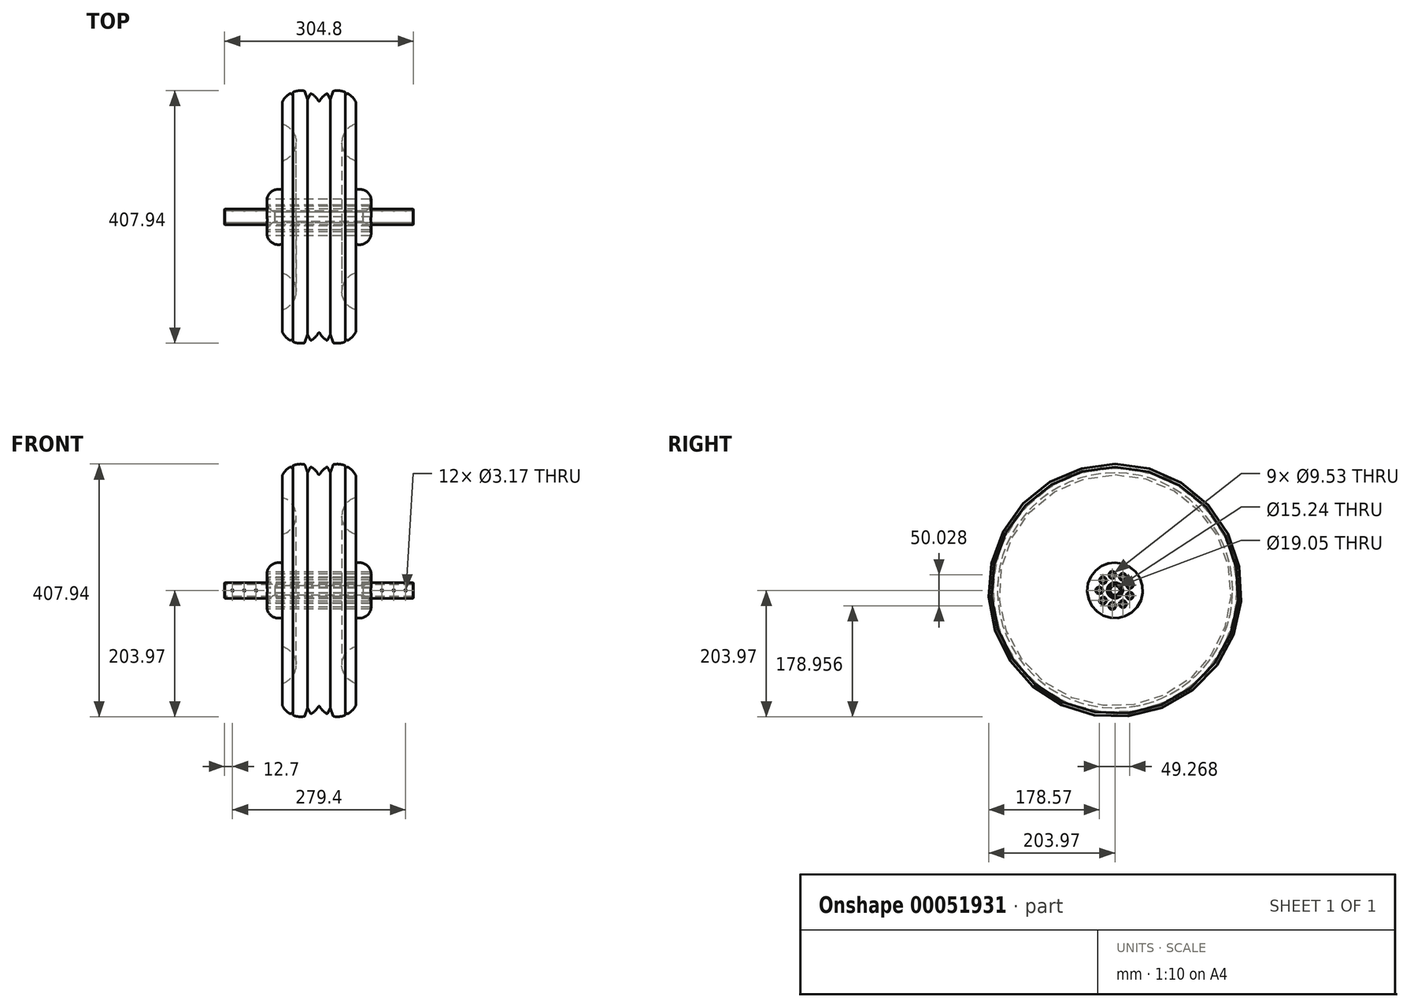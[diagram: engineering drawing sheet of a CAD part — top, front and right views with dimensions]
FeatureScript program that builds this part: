
annotation { "Feature Type Name" : "Feature", "Feature Type Description" : "" }
export const myFeature = defineFeature(function(context is Context, id is Id, definition is map)
    precondition{}
    {
        {
            var Q0;
            Q0=qCreatedBy(makeId("Right.planeOp"),FACE);
            var sketch = newSketch(context, id + "F0", { "sketchPlane" : qUnion([Q0])});
            skCircle(sketch, "E0", {"center": v(0, 0) * mm, "radius": 12.7 * mm});
            skCircle(sketch, "E1", {"center": v(0, 0) * mm, "radius": 9.53 * mm});
            skSolve(sketch);
        }
        {
            var Q0;
            Q0=makeQuery(id+"F0.imprint","IMPRINT",FACE,{"disambiguationData":[TD([[makeQuery(id+"F0.imprint","IMPRINT",EDGE,{"derivedFrom":sQuery(id+"F0.wireOp",EDGE,"E0")}),1.0]])]});
            extrude(context, id + "F1", {"entities" : qUnion([Q0]), "endBound" : BoundingType.SYMMETRIC, "depth" : 304.8 * mm});
        }
        {
            var Q0;
            Q0=qCreatedBy(makeId("Front.planeOp"),FACE);
            var sketch = newSketch(context, id + "F2", { "sketchPlane" : qUnion([Q0])});
            skArc(sketch, "E2", {"start": v(-59.42, 43.9) * mm, "mid": v(-83.37, 31.57) * mm, "end": v(-71.03, 7.62) * mm});
            skArc(sketch, "E3", {"start": v(0, 185.42) * mm, "mid": v(-5.59, 193.52) * mm, "end": v(-13.3, 199.62) * mm});
            skLineSegment(sketch, "E4", {"start": v(-71.03, 7.62) * mm, "end": v(0, 7.62) * mm});
            skLineSegment(sketch, "E5", {"start": v(0, 7.62) * mm, "end": v(0, -76.85) * mm, "construction": true});
            skArc(sketch, "E6.MirrorCS", {"start": v(0, 185.42) * mm, "mid": v(5.59, 193.52) * mm, "end": v(13.3, 199.62) * mm});
            skArc(sketch, "E7.MirrorCS", {"start": v(59.42, 43.9) * mm, "mid": v(83.37, 31.57) * mm, "end": v(71.03, 7.62) * mm});
            skLineSegment(sketch, "E8.MirrorCS", {"start": v(71.03, 7.62) * mm, "end": v(0, 7.62) * mm});
            skLineSegment(sketch, "E9", {"start": v(-111.33, 0) * mm, "end": v(105.13, 0) * mm, "construction": true});
            skLineSegment(sketch, "E10", {"start": v(-46.26, 199.53) * mm, "end": v(-42.37, 196.5) * mm});
            skLineSegment(sketch, "E11", {"start": v(-42.37, 196.5) * mm, "end": v(-42.37, 201.45) * mm});
            skArc(sketch, "E12.trimOffspring", {"start": v(-46.26, 199.53) * mm, "mid": v(-53.9, 193.46) * mm, "end": v(-59.42, 185.42) * mm});
            skLineSegment(sketch, "E13", {"start": v(-23, 203.29) * mm, "end": v(-18.35, 189.78) * mm});
            skLineSegment(sketch, "E14", {"start": v(-18.35, 189.78) * mm, "end": v(-13.3, 199.62) * mm});
            skArc(sketch, "E15.trimOffspring", {"start": v(-23, 203.29) * mm, "mid": v(-32.82, 203.83) * mm, "end": v(-42.37, 201.45) * mm});
            skArc(sketch, "E16.MirrorCS", {"start": v(46.26, 199.53) * mm, "mid": v(53.9, 193.46) * mm, "end": v(59.42, 185.42) * mm});
            skLineSegment(sketch, "E17.MirrorCS", {"start": v(46.26, 199.53) * mm, "end": v(42.37, 196.5) * mm});
            skLineSegment(sketch, "E18.MirrorCS", {"start": v(42.37, 196.5) * mm, "end": v(42.37, 201.45) * mm});
            skLineSegment(sketch, "E19.MirrorCS", {"start": v(23, 203.29) * mm, "end": v(18.35, 189.78) * mm});
            skLineSegment(sketch, "E20.MirrorCS", {"start": v(18.35, 189.78) * mm, "end": v(13.3, 199.62) * mm});
            skArc(sketch, "E21.trimOffspring", {"start": v(23, 203.29) * mm, "mid": v(32.82, 203.83) * mm, "end": v(42.37, 201.45) * mm});
            skLineSegment(sketch, "E22", {"start": v(-59.42, 43.9) * mm, "end": v(-59.42, 90.42) * mm});
            skLineSegment(sketch, "E23", {"start": v(59.42, 185.42) * mm, "end": v(59.42, 150.1) * mm});
            skArc(sketch, "E24", {"start": v(-59.42, 90.42) * mm, "mid": v(-36.85, 120.26) * mm, "end": v(-59.42, 150.1) * mm});
            skLineSegment(sketch, "E25.trimOffspring", {"start": v(-59.42, 150.1) * mm, "end": v(-59.42, 185.42) * mm});
            skPoint(sketch, "E26.orphan", {"position": v(0, 77.88) * mm});
            skArc(sketch, "E27.MirrorCS", {"start": v(59.42, 90.42) * mm, "mid": v(36.85, 120.26) * mm, "end": v(59.42, 150.1) * mm});
            skLineSegment(sketch, "E28.trimOffspring", {"start": v(59.42, 90.42) * mm, "end": v(59.42, 43.9) * mm});
            skSolve(sketch);
        }
        {
            var Q0;
            Q0=makeQuery(id+"F2.imprint","IMPRINT",FACE,{"disambiguationData":[TD([[makeQuery(id+"F2.imprint","IMPRINT",EDGE,{"derivedFrom":sQuery(id+"F2.wireOp",EDGE,"E2")}),1.0]])]});
            var Q1;
            Q1=sQuery(id+"F2.wireOp",EDGE,"E9");
            revolve(context, id + "F3", {"entities" : qUnion([Q0]), "axis" : qUnion([Q1]), "revolveType" : RevolveType.FULL});
        }
        {
            var Q0;
            Q0=qCreatedBy(makeId("Right.planeOp"),FACE);
            var sketch = newSketch(context, id + "F4", { "sketchPlane" : qUnion([Q0])});
            skCircle(sketch, "E29", {"center": v(-25.4, 0) * mm, "radius": 4.76 * mm});
            skCircle(sketch, "E30.1.0", {"center": v(-19.46, -16.33) * mm, "radius": 4.76 * mm});
            skCircle(sketch, "E30.2.0", {"center": v(-4.41, -25.01) * mm, "radius": 4.76 * mm});
            skCircle(sketch, "E30.3.0", {"center": v(12.7, -22) * mm, "radius": 4.76 * mm});
            skCircle(sketch, "E30.4.0", {"center": v(23.87, -8.69) * mm, "radius": 4.76 * mm});
            skCircle(sketch, "E30.5.0", {"center": v(23.87, 8.69) * mm, "radius": 4.76 * mm});
            skCircle(sketch, "E30.6.0", {"center": v(12.7, 22) * mm, "radius": 4.76 * mm});
            skCircle(sketch, "E30.7.0", {"center": v(-4.41, 25.01) * mm, "radius": 4.76 * mm});
            skCircle(sketch, "E30.8.0", {"center": v(-19.46, 16.33) * mm, "radius": 4.76 * mm});
            skPoint(sketch, "E30.center", {"position": v(0, 0) * mm});
            skSolve(sketch);
        }
        {
            var Q0;
            Q0 = qSketchRegion(id + "F4", true);
            extrude(context, id + "F5", {"entities" : qUnion([Q0]), "operationType" : NewBodyOperationType.REMOVE, "endBound" : BoundingType.THROUGH_ALL, "depth" : 25.4 * mm, "hasSecondDirection" : true, "secondDirectionBound" : SecondDirectionBoundingType.THROUGH_ALL, "secondDirectionOppositeDirection" : true, "secondDirectionDepth" : 25.4 * mm});
        }
        {
            var Q0;
            Q0=makeQuery(id+"F1.opExtrude","CAP_EDGE",EDGE,{"disambiguationData":[OSD([sQuery(id+"F0.wireOp",EDGE,"E1")])],"isStart":false});
            var Q1;
            Q1=makeQuery(id+"F1.opExtrude","CAP_EDGE",EDGE,{"disambiguationData":[OSD([sQuery(id+"F0.wireOp",EDGE,"E0")])],"isStart":false});
            var Q2;
            Q2=makeQuery(id+"F1.opExtrude","CAP_EDGE",EDGE,{"disambiguationData":[OSD([sQuery(id+"F0.wireOp",EDGE,"E0")])],"isStart":true});
            var Q3;
            Q3=makeQuery(id+"F1.opExtrude","CAP_EDGE",EDGE,{"disambiguationData":[OSD([sQuery(id+"F0.wireOp",EDGE,"E1")])],"isStart":true});
            chamfer(context, id + "F6", {"entities" : qUnion([Q0, Q1, Q2, Q3]), "width" : 0.76 * mm, "tangentPropagation" : true});
        }
        {
            var Q0;
            Q0=makeQuery(id+"F5.boolean.opBoolean","INTERSECT",EDGE,{"derivedFrom":[makeQuery(id+"F3.opRevolve","SWEPT_FACE",FACE,{"disambiguationData":[OSD([sQuery(id+"F2.wireOp",EDGE,"E7.MirrorCS")])]}),makeQuery(id+"F5.opExtrude","SWEPT_FACE",FACE,{"disambiguationData":[OSD([sQuery(id+"F4.wireOp",EDGE,"E30.5.0")])]})]});
            var Q1;
            Q1=makeQuery(id+"F5.boolean.opBoolean","INTERSECT",EDGE,{"derivedFrom":[makeQuery(id+"F3.opRevolve","SWEPT_FACE",FACE,{"disambiguationData":[OSD([sQuery(id+"F2.wireOp",EDGE,"E7.MirrorCS")])]}),makeQuery(id+"F5.opExtrude","SWEPT_FACE",FACE,{"disambiguationData":[OSD([sQuery(id+"F4.wireOp",EDGE,"E30.4.0")])]})]});
            var Q2;
            Q2=makeQuery(id+"F5.boolean.opBoolean","INTERSECT",EDGE,{"derivedFrom":[makeQuery(id+"F3.opRevolve","SWEPT_FACE",FACE,{"disambiguationData":[OSD([sQuery(id+"F2.wireOp",EDGE,"E7.MirrorCS")])]}),makeQuery(id+"F5.opExtrude","SWEPT_FACE",FACE,{"disambiguationData":[OSD([sQuery(id+"F4.wireOp",EDGE,"E30.6.0")])]})]});
            var Q3;
            Q3=makeQuery(id+"F5.boolean.opBoolean","INTERSECT",EDGE,{"derivedFrom":[makeQuery(id+"F3.opRevolve","SWEPT_FACE",FACE,{"disambiguationData":[OSD([sQuery(id+"F2.wireOp",EDGE,"E7.MirrorCS")])]}),makeQuery(id+"F5.opExtrude","SWEPT_FACE",FACE,{"disambiguationData":[OSD([sQuery(id+"F4.wireOp",EDGE,"E30.7.0")])]})]});
            var Q4;
            Q4=makeQuery(id+"F5.boolean.opBoolean","INTERSECT",EDGE,{"derivedFrom":[makeQuery(id+"F3.opRevolve","SWEPT_FACE",FACE,{"disambiguationData":[OSD([sQuery(id+"F2.wireOp",EDGE,"E7.MirrorCS")])]}),makeQuery(id+"F5.opExtrude","SWEPT_FACE",FACE,{"disambiguationData":[OSD([sQuery(id+"F4.wireOp",EDGE,"E30.8.0")])]})]});
            var Q5;
            Q5=makeQuery(id+"F5.boolean.opBoolean","INTERSECT",EDGE,{"derivedFrom":[makeQuery(id+"F3.opRevolve","SWEPT_FACE",FACE,{"disambiguationData":[OSD([sQuery(id+"F2.wireOp",EDGE,"E7.MirrorCS")])]}),makeQuery(id+"F5.opExtrude","SWEPT_FACE",FACE,{"disambiguationData":[OSD([sQuery(id+"F4.wireOp",EDGE,"E29")])]})]});
            var Q6;
            Q6=makeQuery(id+"F5.boolean.opBoolean","INTERSECT",EDGE,{"derivedFrom":[makeQuery(id+"F3.opRevolve","SWEPT_FACE",FACE,{"disambiguationData":[OSD([sQuery(id+"F2.wireOp",EDGE,"E7.MirrorCS")])]}),makeQuery(id+"F5.opExtrude","SWEPT_FACE",FACE,{"disambiguationData":[OSD([sQuery(id+"F4.wireOp",EDGE,"E30.1.0")])]})]});
            var Q7;
            Q7=makeQuery(id+"F5.boolean.opBoolean","INTERSECT",EDGE,{"derivedFrom":[makeQuery(id+"F3.opRevolve","SWEPT_FACE",FACE,{"disambiguationData":[OSD([sQuery(id+"F2.wireOp",EDGE,"E7.MirrorCS")])]}),makeQuery(id+"F5.opExtrude","SWEPT_FACE",FACE,{"disambiguationData":[OSD([sQuery(id+"F4.wireOp",EDGE,"E30.2.0")])]})]});
            var Q8;
            Q8=makeQuery(id+"F5.boolean.opBoolean","INTERSECT",EDGE,{"derivedFrom":[makeQuery(id+"F3.opRevolve","SWEPT_FACE",FACE,{"disambiguationData":[OSD([sQuery(id+"F2.wireOp",EDGE,"E7.MirrorCS")])]}),makeQuery(id+"F5.opExtrude","SWEPT_FACE",FACE,{"disambiguationData":[OSD([sQuery(id+"F4.wireOp",EDGE,"E30.3.0")])]})]});
            var Q9;
            Q9=makeQuery(id+"F5.boolean.opBoolean","INTERSECT",EDGE,{"derivedFrom":[makeQuery(id+"F3.opRevolve","SWEPT_FACE",FACE,{"disambiguationData":[OSD([sQuery(id+"F2.wireOp",EDGE,"E2")])]}),makeQuery(id+"F5.opExtrude","SWEPT_FACE",FACE,{"disambiguationData":[OSD([sQuery(id+"F4.wireOp",EDGE,"E30.4.0")])]})]});
            var Q10;
            Q10=makeQuery(id+"F5.boolean.opBoolean","INTERSECT",EDGE,{"derivedFrom":[makeQuery(id+"F3.opRevolve","SWEPT_FACE",FACE,{"disambiguationData":[OSD([sQuery(id+"F2.wireOp",EDGE,"E2")])]}),makeQuery(id+"F5.opExtrude","SWEPT_FACE",FACE,{"disambiguationData":[OSD([sQuery(id+"F4.wireOp",EDGE,"E30.5.0")])]})]});
            var Q11;
            Q11=makeQuery(id+"F5.boolean.opBoolean","INTERSECT",EDGE,{"derivedFrom":[makeQuery(id+"F3.opRevolve","SWEPT_FACE",FACE,{"disambiguationData":[OSD([sQuery(id+"F2.wireOp",EDGE,"E2")])]}),makeQuery(id+"F5.opExtrude","SWEPT_FACE",FACE,{"disambiguationData":[OSD([sQuery(id+"F4.wireOp",EDGE,"E30.6.0")])]})]});
            var Q12;
            Q12=makeQuery(id+"F5.boolean.opBoolean","INTERSECT",EDGE,{"derivedFrom":[makeQuery(id+"F3.opRevolve","SWEPT_FACE",FACE,{"disambiguationData":[OSD([sQuery(id+"F2.wireOp",EDGE,"E2")])]}),makeQuery(id+"F5.opExtrude","SWEPT_FACE",FACE,{"disambiguationData":[OSD([sQuery(id+"F4.wireOp",EDGE,"E30.7.0")])]})]});
            var Q13;
            Q13=makeQuery(id+"F5.boolean.opBoolean","INTERSECT",EDGE,{"derivedFrom":[makeQuery(id+"F3.opRevolve","SWEPT_FACE",FACE,{"disambiguationData":[OSD([sQuery(id+"F2.wireOp",EDGE,"E2")])]}),makeQuery(id+"F5.opExtrude","SWEPT_FACE",FACE,{"disambiguationData":[OSD([sQuery(id+"F4.wireOp",EDGE,"E30.8.0")])]})]});
            var Q14;
            Q14=makeQuery(id+"F5.boolean.opBoolean","INTERSECT",EDGE,{"derivedFrom":[makeQuery(id+"F3.opRevolve","SWEPT_FACE",FACE,{"disambiguationData":[OSD([sQuery(id+"F2.wireOp",EDGE,"E2")])]}),makeQuery(id+"F5.opExtrude","SWEPT_FACE",FACE,{"disambiguationData":[OSD([sQuery(id+"F4.wireOp",EDGE,"E29")])]})]});
            var Q15;
            Q15=makeQuery(id+"F5.boolean.opBoolean","INTERSECT",EDGE,{"derivedFrom":[makeQuery(id+"F3.opRevolve","SWEPT_FACE",FACE,{"disambiguationData":[OSD([sQuery(id+"F2.wireOp",EDGE,"E2")])]}),makeQuery(id+"F5.opExtrude","SWEPT_FACE",FACE,{"disambiguationData":[OSD([sQuery(id+"F4.wireOp",EDGE,"E30.1.0")])]})]});
            var Q16;
            Q16=makeQuery(id+"F5.boolean.opBoolean","INTERSECT",EDGE,{"derivedFrom":[makeQuery(id+"F3.opRevolve","SWEPT_FACE",FACE,{"disambiguationData":[OSD([sQuery(id+"F2.wireOp",EDGE,"E2")])]}),makeQuery(id+"F5.opExtrude","SWEPT_FACE",FACE,{"disambiguationData":[OSD([sQuery(id+"F4.wireOp",EDGE,"E30.2.0")])]})]});
            var Q17;
            Q17=makeQuery(id+"F5.boolean.opBoolean","INTERSECT",EDGE,{"derivedFrom":[makeQuery(id+"F3.opRevolve","SWEPT_FACE",FACE,{"disambiguationData":[OSD([sQuery(id+"F2.wireOp",EDGE,"E2")])]}),makeQuery(id+"F5.opExtrude","SWEPT_FACE",FACE,{"disambiguationData":[OSD([sQuery(id+"F4.wireOp",EDGE,"E30.3.0")])]})]});
            fillet(context, id + "F7", {"entities" : qUnion([Q0, Q1, Q2, Q3, Q4, Q5, Q6, Q7, Q8, Q9, Q10, Q11, Q12, Q13, Q14, Q15, Q16, Q17]), "radius" : 0.76 * mm, "tangentPropagation" : true, "allowEdgeOverflow" : false});
        }
        {
            var Q0;
            Q0=makeQuery(id+"F3.opRevolve","SWEPT_EDGE",EDGE,{"disambiguationData":[OSD([sQuery(id+"F2.wireOp",EDGE,"E12.trimOffspring"),sQuery(id+"F2.wireOp",EDGE,"E25.trimOffspring")])]});
            var Q1;
            Q1=makeQuery(id+"F3.opRevolve","SWEPT_EDGE",EDGE,{"disambiguationData":[OSD([sQuery(id+"F2.wireOp",EDGE,"E24"),sQuery(id+"F2.wireOp",EDGE,"E25.trimOffspring")])]});
            var Q2;
            Q2=makeQuery(id+"F3.opRevolve","SWEPT_EDGE",EDGE,{"disambiguationData":[OSD([sQuery(id+"F2.wireOp",EDGE,"E22"),sQuery(id+"F2.wireOp",EDGE,"E24")])]});
            var Q3;
            Q3=makeQuery(id+"F3.opRevolve","SWEPT_EDGE",EDGE,{"disambiguationData":[OSD([sQuery(id+"F2.wireOp",EDGE,"E2"),sQuery(id+"F2.wireOp",EDGE,"E22")])]});
            var Q4;
            Q4=makeQuery(id+"F3.opRevolve","SWEPT_EDGE",EDGE,{"disambiguationData":[OSD([sQuery(id+"F2.wireOp",EDGE,"E10"),sQuery(id+"F2.wireOp",EDGE,"E12.trimOffspring")])]});
            var Q5;
            Q5=makeQuery(id+"F3.opRevolve","SWEPT_EDGE",EDGE,{"disambiguationData":[OSD([sQuery(id+"F2.wireOp",EDGE,"E11"),sQuery(id+"F2.wireOp",EDGE,"E15.trimOffspring")])]});
            var Q6;
            Q6=makeQuery(id+"F3.opRevolve","SWEPT_EDGE",EDGE,{"disambiguationData":[OSD([sQuery(id+"F2.wireOp",EDGE,"E13"),sQuery(id+"F2.wireOp",EDGE,"E15.trimOffspring")])]});
            var Q7;
            Q7=makeQuery(id+"F3.opRevolve","SWEPT_EDGE",EDGE,{"disambiguationData":[OSD([sQuery(id+"F2.wireOp",EDGE,"E3"),sQuery(id+"F2.wireOp",EDGE,"E14")])]});
            var Q8;
            Q8=makeQuery(id+"F3.opRevolve","SWEPT_EDGE",EDGE,{"disambiguationData":[OSD([sQuery(id+"F2.wireOp",EDGE,"E3"),sQuery(id+"F2.wireOp",EDGE,"E6.MirrorCS")])]});
            var Q9;
            Q9=makeQuery(id+"F3.opRevolve","SWEPT_EDGE",EDGE,{"disambiguationData":[OSD([sQuery(id+"F2.wireOp",EDGE,"E6.MirrorCS"),sQuery(id+"F2.wireOp",EDGE,"E20.MirrorCS")])]});
            var Q10;
            Q10=makeQuery(id+"F3.opRevolve","SWEPT_EDGE",EDGE,{"disambiguationData":[OSD([sQuery(id+"F2.wireOp",EDGE,"E19.MirrorCS"),sQuery(id+"F2.wireOp",EDGE,"E21.trimOffspring")])]});
            var Q11;
            Q11=makeQuery(id+"F3.opRevolve","SWEPT_EDGE",EDGE,{"disambiguationData":[OSD([sQuery(id+"F2.wireOp",EDGE,"E18.MirrorCS"),sQuery(id+"F2.wireOp",EDGE,"E21.trimOffspring")])]});
            var Q12;
            Q12=makeQuery(id+"F3.opRevolve","SWEPT_EDGE",EDGE,{"disambiguationData":[OSD([sQuery(id+"F2.wireOp",EDGE,"E17.MirrorCS"),sQuery(id+"F2.wireOp",EDGE,"E16.MirrorCS")])]});
            var Q13;
            Q13=makeQuery(id+"F3.opRevolve","SWEPT_EDGE",EDGE,{"disambiguationData":[OSD([sQuery(id+"F2.wireOp",EDGE,"E16.MirrorCS"),sQuery(id+"F2.wireOp",EDGE,"E23")])]});
            var Q14;
            Q14=makeQuery(id+"F3.opRevolve","SWEPT_EDGE",EDGE,{"disambiguationData":[OSD([sQuery(id+"F2.wireOp",EDGE,"E23"),sQuery(id+"F2.wireOp",EDGE,"E27.MirrorCS")])]});
            var Q15;
            Q15=makeQuery(id+"F3.opRevolve","SWEPT_EDGE",EDGE,{"disambiguationData":[OSD([sQuery(id+"F2.wireOp",EDGE,"E27.MirrorCS"),sQuery(id+"F2.wireOp",EDGE,"E28.trimOffspring")])]});
            var Q16;
            Q16=makeQuery(id+"F3.opRevolve","SWEPT_EDGE",EDGE,{"disambiguationData":[OSD([sQuery(id+"F2.wireOp",EDGE,"E7.MirrorCS"),sQuery(id+"F2.wireOp",EDGE,"E28.trimOffspring")])]});
            fillet(context, id + "F8", {"entities" : qUnion([Q0, Q1, Q2, Q3, Q4, Q5, Q6, Q7, Q8, Q9, Q10, Q11, Q12, Q13, Q14, Q15, Q16]), "radius" : 1.27 * mm, "tangentPropagation" : true, "allowEdgeOverflow" : false});
        }
        {
            var Q0;
            Q0=qCreatedBy(makeId("Front.planeOp"),FACE);
            var sketch = newSketch(context, id + "F9", { "sketchPlane" : qUnion([Q0])});
            skCircle(sketch, "E31", {"center": v(-139.7, 0) * mm, "radius": 1.59 * mm});
            skLineSegment(sketch, "E32", {"start": v(-139.7, 0) * mm, "end": v(0, 0) * mm, "construction": true});
            skCircle(sketch, "E33.1.0.0", {"center": v(-120.65, 0) * mm, "radius": 1.59 * mm});
            skCircle(sketch, "E33.2.0.0", {"center": v(-101.6, 0) * mm, "radius": 1.59 * mm});
            skLineSegment(sketch, "E33.direction1", {"start": v(-139.7, 0) * mm, "end": v(-120.65, 0) * mm, "construction": true});
            skLineSegment(sketch, "E34", {"start": v(0, 0) * mm, "end": v(0, 35.22) * mm});
            skLineSegment(sketch, "E35", {"start": v(0, 35.22) * mm, "end": v(0, -36.48) * mm, "construction": true});
            skCircle(sketch, "E36.MirrorC", {"center": v(139.7, 0) * mm, "radius": 1.59 * mm});
            skCircle(sketch, "E37.MirrorC", {"center": v(120.65, 0) * mm, "radius": 1.59 * mm});
            skCircle(sketch, "E38.MirrorC", {"center": v(101.6, 0) * mm, "radius": 1.59 * mm});
            skSolve(sketch);
        }
        {
            var Q0;
            Q0 = qSketchRegion(id + "F9", true);
            var Q1;
            Q1=sQuery(id+"F9.wireOp",EDGE,"E31");
            extrude(context, id + "F10", {"entities" : qUnion([Q0]), "operationType" : NewBodyOperationType.REMOVE, "surfaceEntities" : qUnion([Q1]), "endBound" : BoundingType.SYMMETRIC, "depth" : 51.55 * mm});
        }
    });
